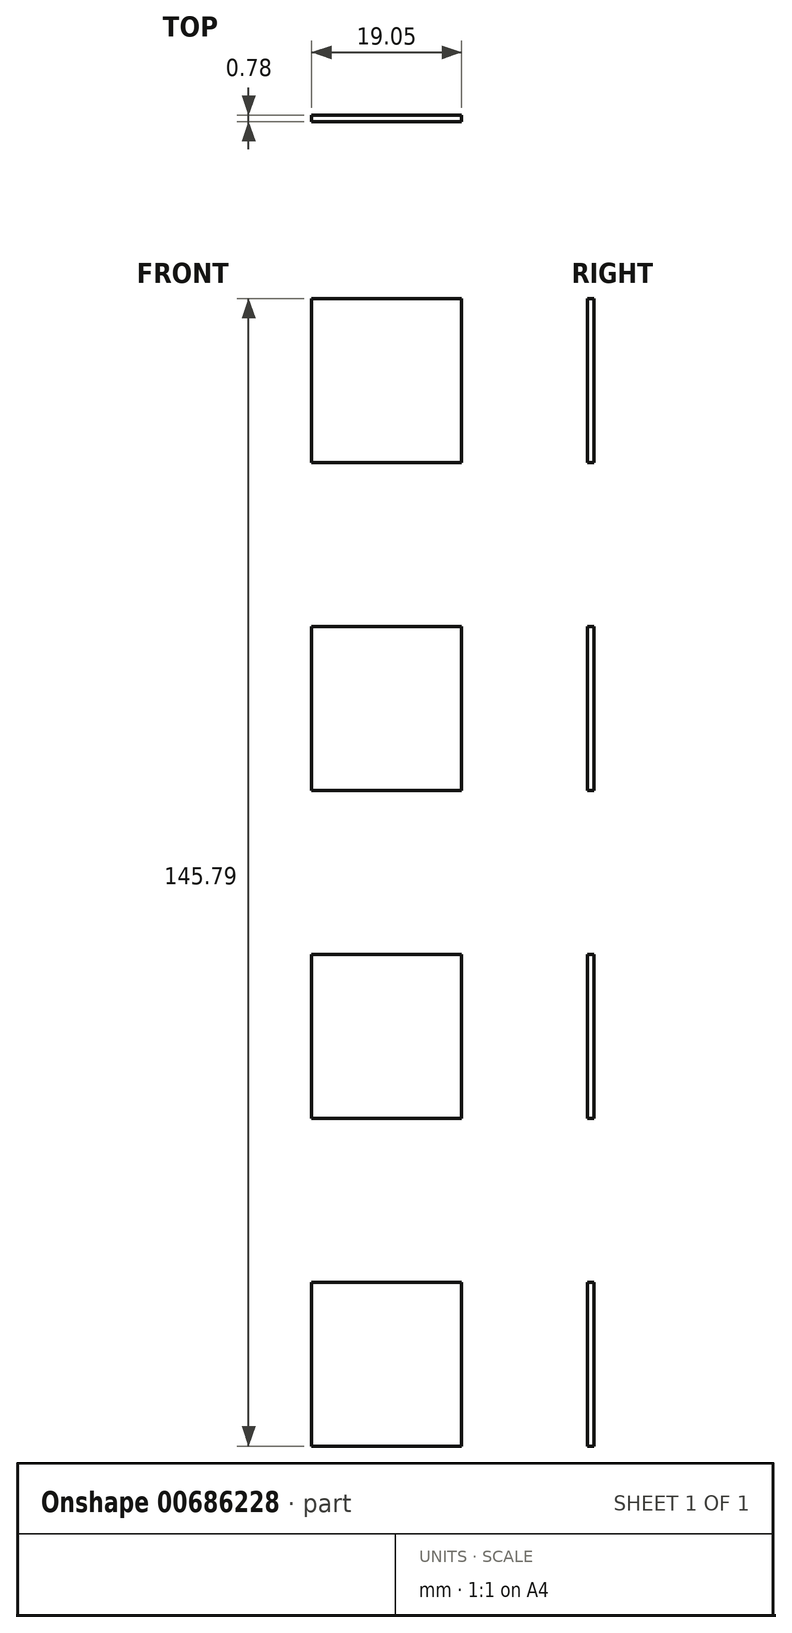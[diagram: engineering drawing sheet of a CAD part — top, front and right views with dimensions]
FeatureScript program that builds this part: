
annotation { "Feature Type Name" : "Feature", "Feature Type Description" : "" }
export const myFeature = defineFeature(function(context is Context, id is Id, definition is map)
    precondition{}
    {
        {
            var Q0;
            Q0=qCreatedBy(makeId("Front.planeOp"),FACE);
            var sketch = newSketch(context, id + "F0", { "sketchPlane" : qUnion([Q0])});
            skLineSegment(sketch, "E0.bottom", {"start": v(0, 0) * mm, "end": v(-19.05, 0) * mm});
            skLineSegment(sketch, "E0.top", {"start": v(0, 166.62) * mm, "end": v(-19.05, 166.62) * mm});
            skLineSegment(sketch, "E0.left", {"start": v(0, 0) * mm, "end": v(0, 166.62) * mm});
            skLineSegment(sketch, "E0.right", {"start": v(-19.05, 0) * mm, "end": v(-19.05, 166.62) * mm});
            skSolve(sketch);
        }
        {
            var Q0;
            Q0=qSketchRegion(id+"F0",true);
            extrude(context, id + "F1", {"entities" : qUnion([Q0]), "oppositeDirection" : true, "depth" : 19.88 / 50.8 * mm, "offsetDistance" : 25.4 * mm});
        }
        {
            var Q0;
            Q0=makeQuery(id+"F1.opExtrude","SWEPT_FACE",FACE,{"disambiguationData":[OSD([sQuery(id+"F0.wireOp",EDGE,"E0.right")])]});
            var sketch = newSketch(context, id + "F2", { "sketchPlane" : qUnion([Q0])});
            skLineSegment(sketch, "E1", {"start": v(-19.05, 166.62) * mm, "end": v(-19.05, 145.8) * mm});
            skLineSegment(sketch, "E2", {"start": v(-19.05, 145.8) * mm, "end": v(-19.05, 124.97) * mm});
            skLineSegment(sketch, "E3", {"start": v(-19.05, 124.97) * mm, "end": v(-19.05, 104.14) * mm});
            skLineSegment(sketch, "E4", {"start": v(-19.05, 104.14) * mm, "end": v(-19.05, 83.31) * mm});
            skLineSegment(sketch, "E5", {"start": v(-19.05, 83.31) * mm, "end": v(-19.05, 62.48) * mm});
            skLineSegment(sketch, "E6", {"start": v(-19.05, 62.48) * mm, "end": v(-19.05, 41.66) * mm});
            skLineSegment(sketch, "E7", {"start": v(-19.05, 41.66) * mm, "end": v(-19.05, 20.83) * mm});
            skLineSegment(sketch, "E8", {"start": v(-19.05, 20.83) * mm, "end": v(-19.05, 0) * mm});
            skSolve(sketch);
        }
        {
            var Q0;
            Q0=qCreatedBy(makeId("Right.planeOp"),FACE);
            var sketch = newSketch(context, id + "F3", { "sketchPlane" : qUnion([Q0])});
            skLineSegment(sketch, "E9.bottom", {"start": v(19.05, 145.8) * mm, "end": v(0, 145.8) * mm, "construction": true});
            skLineSegment(sketch, "E9.top", {"start": v(19.05, 166.62) * mm, "end": v(0, 166.62) * mm, "construction": true});
            skLineSegment(sketch, "E9.left", {"start": v(19.05, 145.8) * mm, "end": v(19.05, 166.62) * mm, "construction": true});
            skLineSegment(sketch, "E9.right", {"start": v(0, 145.8) * mm, "end": v(0, 166.62) * mm, "construction": true});
            skLineSegment(sketch, "E10.bottom", {"start": v(19.05, 124.97) * mm, "end": v(0, 124.97) * mm, "construction": true});
            skLineSegment(sketch, "E10.top", {"start": v(19.05, 104.14) * mm, "end": v(0, 104.14) * mm, "construction": true});
            skLineSegment(sketch, "E10.left", {"start": v(19.05, 124.97) * mm, "end": v(19.05, 104.14) * mm, "construction": true});
            skLineSegment(sketch, "E10.right", {"start": v(0, 124.97) * mm, "end": v(0, 104.14) * mm, "construction": true});
            skLineSegment(sketch, "E11.bottom", {"start": v(19.05, 83.31) * mm, "end": v(0, 83.31) * mm, "construction": true});
            skLineSegment(sketch, "E11.top", {"start": v(19.05, 0) * mm, "end": v(0, 0) * mm, "construction": true});
            skLineSegment(sketch, "E11.left", {"start": v(19.05, 83.31) * mm, "end": v(19.05, 0) * mm, "construction": true});
            skLineSegment(sketch, "E11.right", {"start": v(0, 83.31) * mm, "end": v(0, 0) * mm, "construction": true});
            skLineSegment(sketch, "E12.bottom", {"start": v(19.05, 145.8) * mm, "end": v(0, 145.8) * mm});
            skLineSegment(sketch, "E12.top", {"start": v(19.05, 124.97) * mm, "end": v(0, 124.97) * mm});
            skLineSegment(sketch, "E12.left", {"start": v(19.05, 145.8) * mm, "end": v(19.05, 124.97) * mm});
            skLineSegment(sketch, "E12.right", {"start": v(0, 145.8) * mm, "end": v(0, 124.97) * mm});
            skLineSegment(sketch, "E13.bottom", {"start": v(19.05, 104.14) * mm, "end": v(0, 104.14) * mm});
            skLineSegment(sketch, "E13.top", {"start": v(19.05, 83.31) * mm, "end": v(0, 83.31) * mm});
            skLineSegment(sketch, "E13.left", {"start": v(19.05, 104.14) * mm, "end": v(19.05, 83.31) * mm});
            skLineSegment(sketch, "E13.right", {"start": v(0, 104.14) * mm, "end": v(0, 83.31) * mm});
            skLineSegment(sketch, "E14.bottom", {"start": v(0, 62.48) * mm, "end": v(19.05, 62.48) * mm});
            skLineSegment(sketch, "E14.top", {"start": v(0, 41.66) * mm, "end": v(19.05, 41.66) * mm});
            skLineSegment(sketch, "E14.left", {"start": v(0, 62.48) * mm, "end": v(0, 41.66) * mm});
            skLineSegment(sketch, "E14.right", {"start": v(19.05, 62.48) * mm, "end": v(19.05, 41.66) * mm});
            skLineSegment(sketch, "E15.bottom", {"start": v(0, 20.83) * mm, "end": v(19.05, 20.83) * mm});
            skLineSegment(sketch, "E15.top", {"start": v(0, 0) * mm, "end": v(19.05, 0) * mm});
            skLineSegment(sketch, "E15.left", {"start": v(0, 20.83) * mm, "end": v(0, 0) * mm});
            skLineSegment(sketch, "E15.right", {"start": v(19.05, 20.83) * mm, "end": v(19.05, 0) * mm});
            skSolve(sketch);
        }
        {
            var Q0;
            Q0=qSketchRegion(id+"F3",true);
            extrude(context, id + "F4", {"entities" : qUnion([Q0]), "operationType" : NewBodyOperationType.REMOVE, "endBound" : BoundingType.THROUGH_ALL, "oppositeDirection" : true, "depth" : 25.4 * mm, "offsetDistance" : 25.4 * mm});
        }
        {
            var Q0;
            Q0=makeQuery(id+"F1.opExtrude","SWEPT_BODY",BODY,{"disambiguationData":[OSD([sQuery(id+"F0.wireOp",EDGE,"E0.bottom"),sQuery(id+"F0.wireOp",EDGE,"E0.top"),sQuery(id+"F0.wireOp",EDGE,"E0.left"),sQuery(id+"F0.wireOp",EDGE,"E0.right")])]});
            var Q1;
            Q1=makeQuery(id+"F1.opExtrude","CAP_FACE",FACE,{"disambiguationData":[OSD([sQuery(id+"F0.wireOp",EDGE,"E0.bottom"),sQuery(id+"F0.wireOp",EDGE,"E0.top"),sQuery(id+"F0.wireOp",EDGE,"E0.left"),sQuery(id+"F0.wireOp",EDGE,"E0.right")])],"isStart":false});
            mirror(context, id + "F5", {"operationType" : NewBodyOperationType.ADD, "entities" : qUnion([Q0]), "mirrorPlane" : qUnion([Q1])});
        }
        {
            var Q0;
            Q0=qCreatedBy(makeId("Top.planeOp"),FACE);
            cPlane(context, id + "F6", {"entities" : qUnion([Q0]), "cplaneType" : CPlaneType.OFFSET, "offset" : 76.2 * mm, "width" : 152.4 * mm, "height" : 152.4 * mm});
        }
        {
            var Q0;
            Q0=qCreatedBy(id+"F6.planeOp",FACE);
            var sketch = newSketch(context, id + "F7", { "sketchPlane" : qUnion([Q0])});
            skCircle(sketch, "E16", {"center": v(-111.12, 252.41) * mm, "radius": 101.6 * mm});
            skPoint(sketch, "E17", {"position": v(-9.52, 252.41) * mm});
            skLineSegment(sketch, "E18", {"start": v(-9.52, 252.41) * mm, "end": v(-19.05, 252.41) * mm, "construction": true});
            skSolve(sketch);
        }
        {
            var Q0;
            Q0 = qSketchRegion(id + "F7", true);
            extrude(context, id + "F8", {"entities" : qUnion([Q0]), "operationType" : NewBodyOperationType.REMOVE, "endBound" : BoundingType.SYMMETRIC, "oppositeDirection" : true, "depth" : 20.98 * mm, "offsetDistance" : 25.4 * mm});
        }
    });
